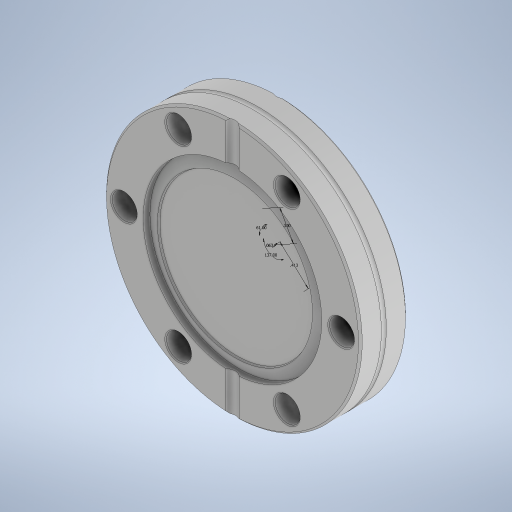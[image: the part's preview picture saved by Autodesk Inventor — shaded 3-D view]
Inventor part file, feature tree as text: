
AUTODESK INVENTOR PART (.ipt)
format: ipt  version: 2024 (Build 280153000, 153)  size: 354,304 bytes
history: native  units: in
note: dims shown in document units (in); Inventor stores cm internally (conversion verified against a paired STEP export)
features: sketch x1
ambient origin geometry x8: Origin, YZ Plane, XZ Plane, XY Plane, X Axis, Y Axis, Z Axis, Center Point
bodies: Solid1 (feature_tree)
feature tree (1):
  sketch  "Sketch1"  dims[d1=0.3001in d2=0.4192in d3=0.0625in d4=0.4126in d5=0.9414in]
